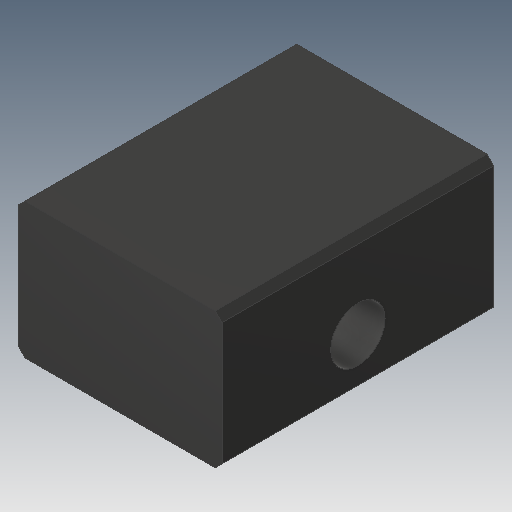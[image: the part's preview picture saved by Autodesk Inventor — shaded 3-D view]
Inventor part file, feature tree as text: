
AUTODESK INVENTOR PART (.ipt)
format: ipt  version: 2018 (Build 220112000, 112)  size: 99,328 bytes
history: native  units: in
note: dims shown in document units (in); Inventor stores cm internally (conversion verified against a paired STEP export)
features: other x3, sketch x1
ambient origin geometry x8: Origin, YZ Plane, XZ Plane, XY Plane, X Axis, Y Axis, Z Axis, Center Point
bodies: Solid1 (feature_tree)
feature tree (4):
  other  "10-006-ACTR-FIX.ipt"
  other  "Solid1::10-006-ACTR-FIX.ipt"
  other  "TaggingFeature1"
  sketch  "Sketch1"  dims[d0=0.3937in]
